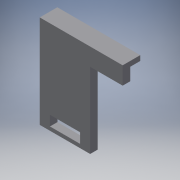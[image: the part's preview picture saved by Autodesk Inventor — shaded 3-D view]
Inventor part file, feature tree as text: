
AUTODESK INVENTOR PART (.ipt)
format: ipt  version: 2019 (Build 230136000, 136)  size: 168,960 bytes
history: native  units: mm
features: extrude x6, sketch x6, projected_geometry x4, other x3, reference x2, chamfer x1
ambient origin geometry x8: Origin, YZ Plane, XZ Plane, XY Plane, X Axis, Y Axis, Z Axis, Center Point
bodies: Solid1 (feature_tree)
feature tree (22):
  extrude  "Extrusion1"  Depth=3.0mm TaperAngle=0.0deg
  extrude  "Extrusion2"  Depth=4.0mm
  extrude  "Extrusion3"  Depth=12.0mm
  extrude  "Extrusion5"  Depth=4.0mm
  chamfer  "Chamfer1"  Distance=4.0mm
  extrude  "Extrusion6"  Depth=2.0mm
  extrude  "Extrusion4"  Depth=4.0mm
  sketch  "Sketch1"  dims[d1=45.0mm d2=3.0mm d3=0.0mm]
  reference  "Reference1"
  sketch  "Sketch2"  dims[d4=4.0mm d5=0.0mm d7=45.842722mm]
  reference  "Reference2"
  projected_geometry  "Projected Loop1"
  sketch  "Sketch3"  dims[d8=22.93mm d9=12.0mm]
  sketch  "Sketch4"  dims[d10=4.0mm d11=4.0mm]
  projected_geometry  "Projected Loop2"
  sketch  "Sketch5"  dims[d12=3.5mm]
  projected_geometry  "Projected Loop3"
  sketch  "Sketch6"  dims[d13=3.5mm d21=4.0mm d22=0.0mm d23=22.93mm d24=4.0mm d25=4.0mm d26=3.0mm d27=5.0mm d28=40.0mm d30=9.0mm d31=10.0mm d33=10.0mm d35=13.0mm d36=0.0mm d37=4.0mm d38=0.0mm d39=30.0mm d40=4.0mm d41=8.75mm d42=2.0mm d43=45.0deg d44=8.0mm d45=12.5mm d46=0.0mm]
  projected_geometry  "Projected Loop4"
  parser-record x1  (decoder bookkeeping rows leaked as tree rows — omitted from the tree; the rows remain in map.json)
  other  "Aligner Helper Assembly.iam"
  other  "Base v6 - 175:2"
note: 1 file-system path scrubbed to <path> (originals preserved in map.json)
